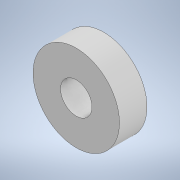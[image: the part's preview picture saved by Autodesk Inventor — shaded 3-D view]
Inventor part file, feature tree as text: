
AUTODESK INVENTOR PART (.ipt)
format: ipt  version: 2022.2 (Build 262287010, 287A)  size: 97,792 bytes
history: native  units: mm
features: extrude x1, sketch x1
ambient origin geometry x8: Origin, YZ Plane, XZ Plane, XY Plane, X Axis, Y Axis, Z Axis, Center Point
bodies: Solid1 (feature_tree)
feature tree (2):
  extrude  "Extrusion1"  Depth=7.0mm
  sketch  "Sketch1"  dims[d0=22.0mm d1=8.0mm d2=7.0mm d3=0.0mm]
